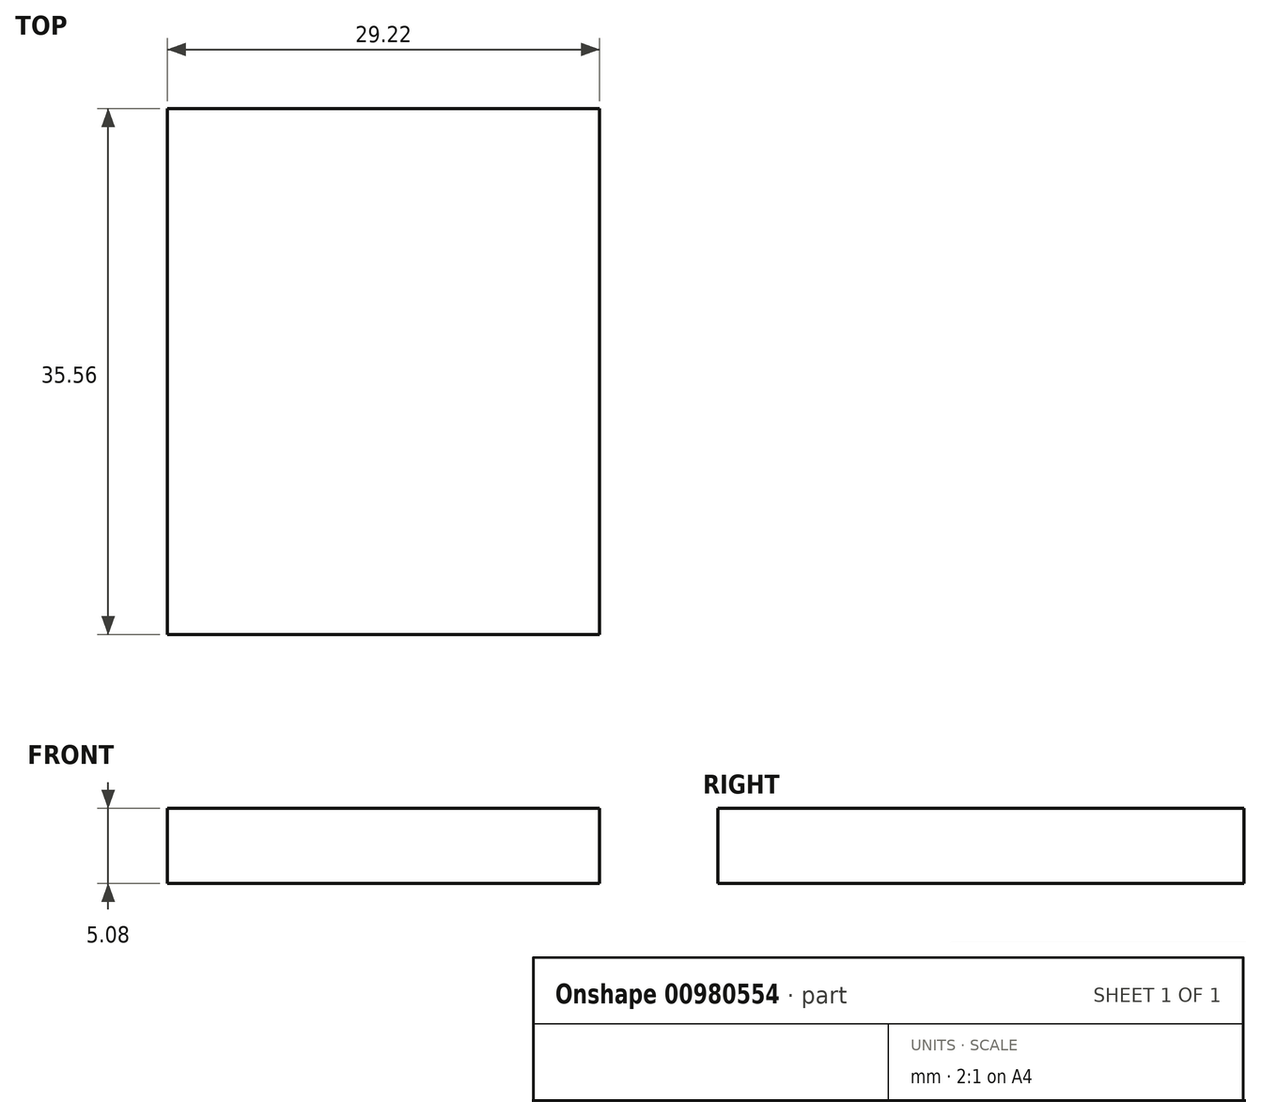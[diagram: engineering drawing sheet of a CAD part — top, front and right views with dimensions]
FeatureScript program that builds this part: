
annotation { "Feature Type Name" : "Feature", "Feature Type Description" : "" }
export const myFeature = defineFeature(function(context is Context, id is Id, definition is map)
    precondition{}
    {
        {
            var Q0;
            Q0=qCreatedBy(makeId("Top.planeOp"),FACE);
            var sketch = newSketch(context, id + "F0", { "sketchPlane" : qUnion([Q0])});
            skLineSegment(sketch, "E0.bottom", {"start": v(14.6, 17.78) * mm, "end": v(-14.6, 17.78) * mm});
            skLineSegment(sketch, "E0.top", {"start": v(14.6, -17.78) * mm, "end": v(-14.6, -17.78) * mm});
            skLineSegment(sketch, "E0.left", {"start": v(14.6, 17.78) * mm, "end": v(14.6, -17.78) * mm});
            skLineSegment(sketch, "E0.right", {"start": v(-14.6, 17.78) * mm, "end": v(-14.6, -17.78) * mm});
            skPoint(sketch, "E0.middle", {"position": v(0, 0) * mm});
            skSolve(sketch);
        }
        {
            var Q0;
            Q0=makeQuery(id+"F0.imprint","IMPRINT",FACE,{"disambiguationData":[TD([[makeQuery(id+"F0.imprint","IMPRINT",EDGE,{"derivedFrom":sQuery(id+"F0.wireOp",EDGE,"E0.bottom")}),1.0]])]});
            extrude(context, id + "F1", {"entities" : qUnion([Q0]), "depth" : 5.08 * mm, "offsetDistance" : 25.4 * mm});
        }
    });
